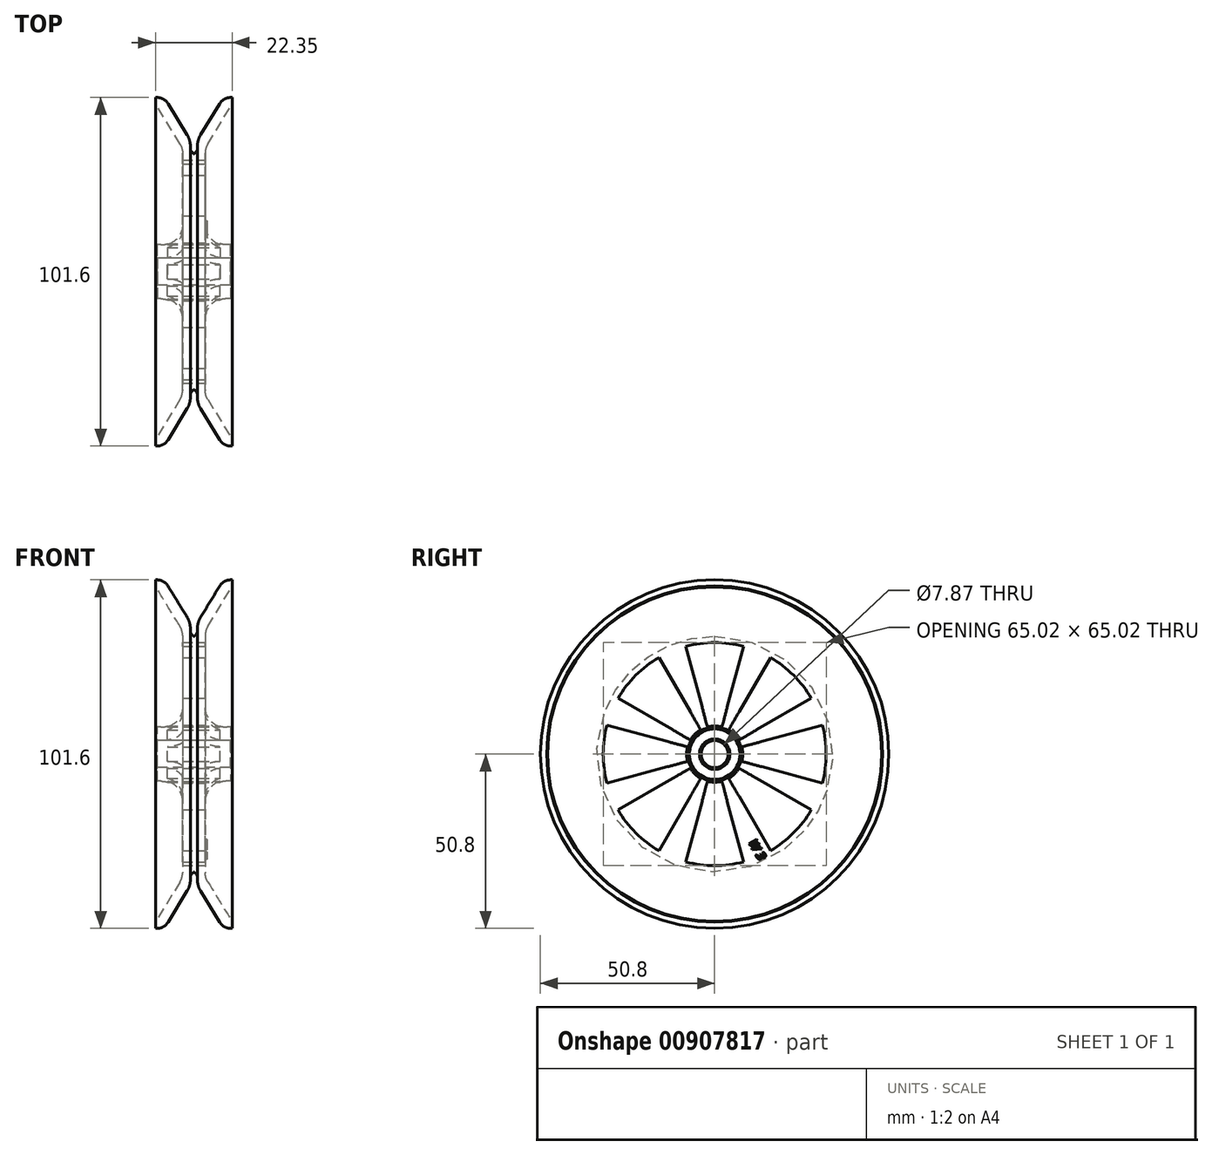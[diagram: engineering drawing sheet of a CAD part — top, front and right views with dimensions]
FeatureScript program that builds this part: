
annotation { "Feature Type Name" : "Feature", "Feature Type Description" : "" }
export const myFeature = defineFeature(function(context is Context, id is Id, definition is map)
    precondition{}
    {
        {
            var Q0;
            Q0=qCreatedBy(makeId("Front.planeOp"),FACE);
            var sketch = newSketch(context, id + "F0", { "sketchPlane" : qUnion([Q0])});
            skLineSegment(sketch, "E0", {"start": v(0, 0) * mm, "end": v(19.05, 0) * mm, "construction": true});
            skLineSegment(sketch, "E1", {"start": v(0, 50.8) * mm, "end": v(0, 48.87) * mm});
            skLineSegment(sketch, "E2", {"start": v(0, 3.94) * mm, "end": v(11.18, 3.94) * mm});
            skLineSegment(sketch, "E3", {"start": v(0, 50.8) * mm, "end": v(0.4, 50.8) * mm});
            skLineSegment(sketch, "E4", {"start": v(3.65, 48.98) * mm, "end": v(9.23, 39.88) * mm});
            skLineSegment(sketch, "E5", {"start": v(10.16, 36.56) * mm, "end": v(10.16, 35.83) * mm});
            skLineSegment(sketch, "E6", {"start": v(11.18, 43.14) * mm, "end": v(11.18, -8.37) * mm, "construction": true});
            skLineSegment(sketch, "E7", {"start": v(10.53, 34.93) * mm, "end": v(11.03, 34.43) * mm});
            skPoint(sketch, "E8.visualSharp", {"position": v(10.16, 38.35) * mm});
            skArc(sketch, "E8.filletArc", {"start": v(10.16, 36.56) * mm, "mid": v(9.92, 38.29) * mm, "end": v(9.23, 39.88) * mm});
            skPoint(sketch, "E9.visualSharp", {"position": v(10.16, 35.3) * mm});
            skArc(sketch, "E9.filletArc", {"start": v(10.16, 35.83) * mm, "mid": v(10.26, 35.35) * mm, "end": v(10.53, 34.93) * mm});
            skPoint(sketch, "E10.visualSharp", {"position": v(2.54, 50.8) * mm});
            skArc(sketch, "E10.filletArc", {"start": v(3.65, 48.98) * mm, "mid": v(2.27, 50.31) * mm, "end": v(0.4, 50.8) * mm});
            skLineSegment(sketch, "E11.MirrorCS", {"start": v(12.2, 36.56) * mm, "end": v(12.2, 35.83) * mm});
            skLineSegment(sketch, "E12.MirrorCS", {"start": v(11.82, 34.93) * mm, "end": v(11.32, 34.43) * mm});
            skArc(sketch, "E13.MirrorCS", {"start": v(12.2, 35.83) * mm, "mid": v(12.1, 35.35) * mm, "end": v(11.82, 34.93) * mm});
            skArc(sketch, "E14.MirrorCS", {"start": v(12.2, 36.56) * mm, "mid": v(12.43, 38.29) * mm, "end": v(13.13, 39.88) * mm});
            skLineSegment(sketch, "E15.MirrorCS", {"start": v(22.35, 50.8) * mm, "end": v(21.95, 50.8) * mm});
            skArc(sketch, "E16.MirrorCS", {"start": v(18.7, 48.98) * mm, "mid": v(20.08, 50.31) * mm, "end": v(21.95, 50.8) * mm});
            skLineSegment(sketch, "E17.MirrorCS", {"start": v(18.7, 48.98) * mm, "end": v(13.13, 39.88) * mm});
            skPoint(sketch, "E18.MirrorP", {"position": v(19.81, 50.8) * mm});
            skLineSegment(sketch, "E19.MirrorCS", {"start": v(22.35, 50.8) * mm, "end": v(22.35, 48.87) * mm});
            skLineSegment(sketch, "E20.MirrorCS", {"start": v(22.35, 3.94) * mm, "end": v(11.18, 3.94) * mm});
            skPoint(sketch, "E21.MirrorP", {"position": v(12.2, 38.35) * mm});
            skPoint(sketch, "E22.MirrorP", {"position": v(12.2, 35.3) * mm});
            skPoint(sketch, "E23.visualSharp", {"position": v(11.18, 34.3) * mm});
            skArc(sketch, "E23.filletArc", {"start": v(11.03, 34.43) * mm, "mid": v(11.18, 34.37) * mm, "end": v(11.32, 34.43) * mm});
            skLineSegment(sketch, "E24", {"start": v(0, 7.87) * mm, "end": v(1.52, 7.87) * mm});
            skLineSegment(sketch, "E25", {"start": v(7.87, 14.22) * mm, "end": v(7.87, 36) * mm});
            skLineSegment(sketch, "E26", {"start": v(7.87, 36) * mm, "end": v(0, 48.87) * mm});
            skLineSegment(sketch, "E27.trimOffspring", {"start": v(0, 7.87) * mm, "end": v(0, 3.94) * mm});
            skLineSegment(sketch, "E28.MirrorCS", {"start": v(14.48, 36) * mm, "end": v(22.35, 48.87) * mm});
            skLineSegment(sketch, "E29.MirrorCS", {"start": v(14.48, 14.22) * mm, "end": v(14.48, 36) * mm});
            skLineSegment(sketch, "E30.MirrorCS", {"start": v(22.35, 7.87) * mm, "end": v(20.83, 7.87) * mm});
            skLineSegment(sketch, "E31.trimOffspring", {"start": v(22.35, 7.87) * mm, "end": v(22.35, 3.94) * mm});
            skPoint(sketch, "E32.visualSharp", {"position": v(14.48, 7.87) * mm});
            skArc(sketch, "E32.filletArc", {"start": v(14.48, 14.22) * mm, "mid": v(16.34, 9.73) * mm, "end": v(20.83, 7.87) * mm});
            skPoint(sketch, "E33.visualSharp", {"position": v(7.87, 7.87) * mm});
            skArc(sketch, "E33.filletArc", {"start": v(1.52, 7.87) * mm, "mid": v(6.01, 9.73) * mm, "end": v(7.87, 14.22) * mm});
            skSolve(sketch);
        }
        {
            var Q0;
            Q0=qSketchRegion(id+"F0",true);
            var Q1;
            Q1=sQuery(id+"F0.wireOp",EDGE,"E0");
            revolve(context, id + "F1", {"surfaceOperationType" : NewSurfaceOperationType.NEW, "entities" : qUnion([Q0]), "axis" : qUnion([Q1]), "revolveType" : RevolveType.FULL});
        }
        {
            var Q0;
            Q0=makeQuery(id+"F1.opRevolve","SWEPT_FACE",FACE,{"disambiguationData":[OSD([sQuery(id+"F0.wireOp",EDGE,"E29.MirrorCS")])]});
            var sketch = newSketch(context, id + "F2", { "sketchPlane" : qUnion([Q0])});
            skArc(sketch, "E34", {"start": v(0, 32.51) * mm, "mid": v(-4.24, 32.23) * mm, "end": v(-8.41, 31.4) * mm});
            skArc(sketch, "E35", {"start": v(0, 8.18) * mm, "mid": v(-1.07, 8.11) * mm, "end": v(-2.12, 7.9) * mm});
            skLineSegment(sketch, "E36", {"start": v(0, 35.5) * mm, "end": v(0, 4.54) * mm, "construction": true});
            skLineSegment(sketch, "E37", {"start": v(-2.12, 7.9) * mm, "end": v(-8.41, 31.4) * mm});
            skArc(sketch, "E38.MirrorCS", {"start": v(0, 32.51) * mm, "mid": v(4.24, 32.23) * mm, "end": v(8.41, 31.4) * mm});
            skLineSegment(sketch, "E39.MirrorCS", {"start": v(2.12, 7.9) * mm, "end": v(8.41, 31.4) * mm});
            skArc(sketch, "E40.MirrorCS", {"start": v(0, 8.18) * mm, "mid": v(1.07, 8.11) * mm, "end": v(2.12, 7.9) * mm});
            skLineSegment(sketch, "E41.1.0", {"start": v(-7.08, 4.1) * mm, "end": v(-28.16, 16.26) * mm});
            skArc(sketch, "E41.1.1", {"start": v(-22.99, 22.99) * mm, "mid": v(-25.8, 19.8) * mm, "end": v(-28.16, 16.26) * mm});
            skArc(sketch, "E41.1.2", {"start": v(-5.78, 5.78) * mm, "mid": v(-6.5, 4.98) * mm, "end": v(-7.08, 4.1) * mm});
            skArc(sketch, "E41.1.3", {"start": v(-5.78, 5.78) * mm, "mid": v(-4.98, 6.5) * mm, "end": v(-4.1, 7.08) * mm});
            skLineSegment(sketch, "E41.1.4", {"start": v(-4.1, 7.08) * mm, "end": v(-16.26, 28.16) * mm});
            skArc(sketch, "E41.1.5", {"start": v(-22.99, 22.99) * mm, "mid": v(-19.8, 25.8) * mm, "end": v(-16.26, 28.16) * mm});
            skLineSegment(sketch, "E41.2.0", {"start": v(-7.9, -2.12) * mm, "end": v(-31.4, -8.41) * mm});
            skArc(sketch, "E41.2.1", {"start": v(-32.51, 0) * mm, "mid": v(-32.23, -4.24) * mm, "end": v(-31.4, -8.41) * mm});
            skArc(sketch, "E41.2.2", {"start": v(-8.18, 0) * mm, "mid": v(-8.11, -1.07) * mm, "end": v(-7.9, -2.12) * mm});
            skArc(sketch, "E41.2.3", {"start": v(-8.18, 0) * mm, "mid": v(-8.11, 1.07) * mm, "end": v(-7.9, 2.12) * mm});
            skLineSegment(sketch, "E41.2.4", {"start": v(-7.9, 2.12) * mm, "end": v(-31.4, 8.41) * mm});
            skArc(sketch, "E41.2.5", {"start": v(-32.51, 0) * mm, "mid": v(-32.23, 4.24) * mm, "end": v(-31.4, 8.41) * mm});
            skLineSegment(sketch, "E42.1.3.0", {"start": v(-4.1, -7.08) * mm, "end": v(-16.26, -28.16) * mm});
            skArc(sketch, "E42.3.3.0", {"start": v(-22.99, -22.99) * mm, "mid": v(-19.8, -25.8) * mm, "end": v(-16.26, -28.16) * mm});
            skArc(sketch, "E42.7.3.0", {"start": v(-5.78, -5.78) * mm, "mid": v(-4.98, -6.5) * mm, "end": v(-4.1, -7.08) * mm});
            skArc(sketch, "E42.11.3.0", {"start": v(-5.78, -5.78) * mm, "mid": v(-6.5, -4.98) * mm, "end": v(-7.08, -4.1) * mm});
            skLineSegment(sketch, "E42.15.3.0", {"start": v(-7.08, -4.1) * mm, "end": v(-28.16, -16.26) * mm});
            skArc(sketch, "E42.18.3.0", {"start": v(-22.99, -22.99) * mm, "mid": v(-25.8, -19.8) * mm, "end": v(-28.16, -16.26) * mm});
            skLineSegment(sketch, "E42.1.4.0", {"start": v(2.12, -7.9) * mm, "end": v(8.41, -31.4) * mm});
            skArc(sketch, "E42.3.4.0", {"start": v(0, -32.51) * mm, "mid": v(4.24, -32.23) * mm, "end": v(8.41, -31.4) * mm});
            skArc(sketch, "E42.7.4.0", {"start": v(0, -8.18) * mm, "mid": v(1.07, -8.11) * mm, "end": v(2.12, -7.9) * mm});
            skArc(sketch, "E42.11.4.0", {"start": v(0, -8.18) * mm, "mid": v(-1.07, -8.11) * mm, "end": v(-2.12, -7.9) * mm});
            skLineSegment(sketch, "E42.15.4.0", {"start": v(-2.12, -7.9) * mm, "end": v(-8.41, -31.4) * mm});
            skArc(sketch, "E42.18.4.0", {"start": v(0, -32.51) * mm, "mid": v(-4.24, -32.23) * mm, "end": v(-8.41, -31.4) * mm});
            skLineSegment(sketch, "E42.1.5.0", {"start": v(7.08, -4.1) * mm, "end": v(28.16, -16.26) * mm});
            skArc(sketch, "E42.3.5.0", {"start": v(22.99, -22.99) * mm, "mid": v(25.8, -19.8) * mm, "end": v(28.16, -16.26) * mm});
            skArc(sketch, "E42.7.5.0", {"start": v(5.78, -5.78) * mm, "mid": v(6.5, -4.98) * mm, "end": v(7.08, -4.1) * mm});
            skArc(sketch, "E42.11.5.0", {"start": v(5.78, -5.78) * mm, "mid": v(4.98, -6.5) * mm, "end": v(4.1, -7.08) * mm});
            skLineSegment(sketch, "E42.15.5.0", {"start": v(4.1, -7.08) * mm, "end": v(16.26, -28.16) * mm});
            skArc(sketch, "E42.18.5.0", {"start": v(22.99, -22.99) * mm, "mid": v(19.8, -25.8) * mm, "end": v(16.26, -28.16) * mm});
            skLineSegment(sketch, "E42.1.6.0", {"start": v(7.9, 2.12) * mm, "end": v(31.4, 8.41) * mm});
            skArc(sketch, "E42.3.6.0", {"start": v(32.51, 0) * mm, "mid": v(32.23, 4.24) * mm, "end": v(31.4, 8.41) * mm});
            skArc(sketch, "E42.7.6.0", {"start": v(8.18, 0) * mm, "mid": v(8.11, 1.07) * mm, "end": v(7.9, 2.12) * mm});
            skArc(sketch, "E42.11.6.0", {"start": v(8.18, 0) * mm, "mid": v(8.11, -1.07) * mm, "end": v(7.9, -2.12) * mm});
            skLineSegment(sketch, "E42.15.6.0", {"start": v(7.9, -2.12) * mm, "end": v(31.4, -8.41) * mm});
            skArc(sketch, "E42.18.6.0", {"start": v(32.51, 0) * mm, "mid": v(32.23, -4.24) * mm, "end": v(31.4, -8.41) * mm});
            skLineSegment(sketch, "E42.1.7.0", {"start": v(4.1, 7.08) * mm, "end": v(16.26, 28.16) * mm});
            skArc(sketch, "E42.3.7.0", {"start": v(22.99, 22.99) * mm, "mid": v(19.8, 25.8) * mm, "end": v(16.26, 28.16) * mm});
            skArc(sketch, "E42.7.7.0", {"start": v(5.78, 5.78) * mm, "mid": v(4.98, 6.5) * mm, "end": v(4.1, 7.08) * mm});
            skArc(sketch, "E42.11.7.0", {"start": v(5.78, 5.78) * mm, "mid": v(6.5, 4.98) * mm, "end": v(7.08, 4.1) * mm});
            skLineSegment(sketch, "E42.15.7.0", {"start": v(7.08, 4.1) * mm, "end": v(28.16, 16.26) * mm});
            skArc(sketch, "E42.18.7.0", {"start": v(22.99, 22.99) * mm, "mid": v(25.8, 19.8) * mm, "end": v(28.16, 16.26) * mm});
            skSolve(sketch);
        }
        {
            var Q0;
            Q0=qSketchRegion(id+"F2",true);
            extrude(context, id + "F3", {"entities" : qUnion([Q0]), "operationType" : NewBodyOperationType.REMOVE, "endBound" : BoundingType.SYMMETRIC, "oppositeDirection" : true, "depth" : 25.4 * mm, "offsetDistance" : 25.4 * mm});
        }
        {
            var Q0;
            Q0=makeQuery(id+"F1.opRevolve","SWEPT_EDGE",EDGE,{"disambiguationData":[OSD([sQuery(id+"F0.wireOp",EDGE,"E20.MirrorCS"),sQuery(id+"F0.wireOp",EDGE,"E31.trimOffspring")])]});
            var Q1;
            Q1=makeQuery(id+"F1.opRevolve","SWEPT_EDGE",EDGE,{"disambiguationData":[OSD([sQuery(id+"F0.wireOp",EDGE,"E30.MirrorCS"),sQuery(id+"F0.wireOp",EDGE,"E31.trimOffspring")])]});
            var Q2;
            Q2=makeQuery(id+"F1.opRevolve","SWEPT_EDGE",EDGE,{"disambiguationData":[OSD([sQuery(id+"F0.wireOp",EDGE,"E2"),sQuery(id+"F0.wireOp",EDGE,"E27.trimOffspring")])]});
            var Q3;
            Q3=makeQuery(id+"F1.opRevolve","SWEPT_EDGE",EDGE,{"disambiguationData":[OSD([sQuery(id+"F0.wireOp",EDGE,"E24"),sQuery(id+"F0.wireOp",EDGE,"E27.trimOffspring")])]});
            var Q4;
            Q4=makeQuery(id+"F1.opRevolve","SWEPT_EDGE",EDGE,{"disambiguationData":[OSD([sQuery(id+"F0.wireOp",EDGE,"E1"),sQuery(id+"F0.wireOp",EDGE,"E26")])]});
            var Q5;
            Q5=makeQuery(id+"F1.opRevolve","SWEPT_EDGE",EDGE,{"disambiguationData":[OSD([sQuery(id+"F0.wireOp",EDGE,"E19.MirrorCS"),sQuery(id+"F0.wireOp",EDGE,"E28.MirrorCS")])]});
            chamfer(context, id + "F4", {"entities" : qUnion([Q0, Q1, Q2, Q3, Q4, Q5]), "width" : 0.5 * mm, "tangentPropagation" : true});
        }
        {
            var Q0;
            Q0=makeQuery(id+"F1.opRevolve","SWEPT_EDGE",EDGE,{"disambiguationData":[OSD([sQuery(id+"F0.wireOp",EDGE,"E25"),sQuery(id+"F0.wireOp",EDGE,"E26")])]});
            var Q1;
            Q1=makeQuery(id+"F1.opRevolve","SWEPT_EDGE",EDGE,{"disambiguationData":[OSD([sQuery(id+"F0.wireOp",EDGE,"E28.MirrorCS"),sQuery(id+"F0.wireOp",EDGE,"E29.MirrorCS")])]});
            fillet(context, id + "F5", {"entities" : qUnion([Q0, Q1]), "radius" : 5.08 * mm, "tangentPropagation" : true, "allowEdgeOverflow" : false});
        }
        {
            var Q0;
            Q0=makeQuery(id+"F1.opRevolve","SWEPT_FACE",FACE,{"disambiguationData":[OSD([sQuery(id+"F0.wireOp",EDGE,"E29.MirrorCS")])]});
            var sketch = newSketch(context, id + "F6", { "sketchPlane" : qUnion([Q0])});
            skText(sketch, "E43", { "text": "W 3", "fontName": "OpenSans-BoldItalic.ttf"});
            const initialGuessF6  = {"E43": [0.00981, -0.0258, 0.5, -0.86603, 0.0026]};
            skSetInitialGuess(sketch, initialGuessF6);
            skSolve(sketch);
        }
        {
            var Q0;
            Q0=qSketchRegion(id+"F6",true);
            extrude(context, id + "F7", {"entities" : qUnion([Q0]), "operationType" : NewBodyOperationType.ADD, "depth" : 0.5 * mm, "offsetDistance" : 25.4 * mm});
        }
    });
